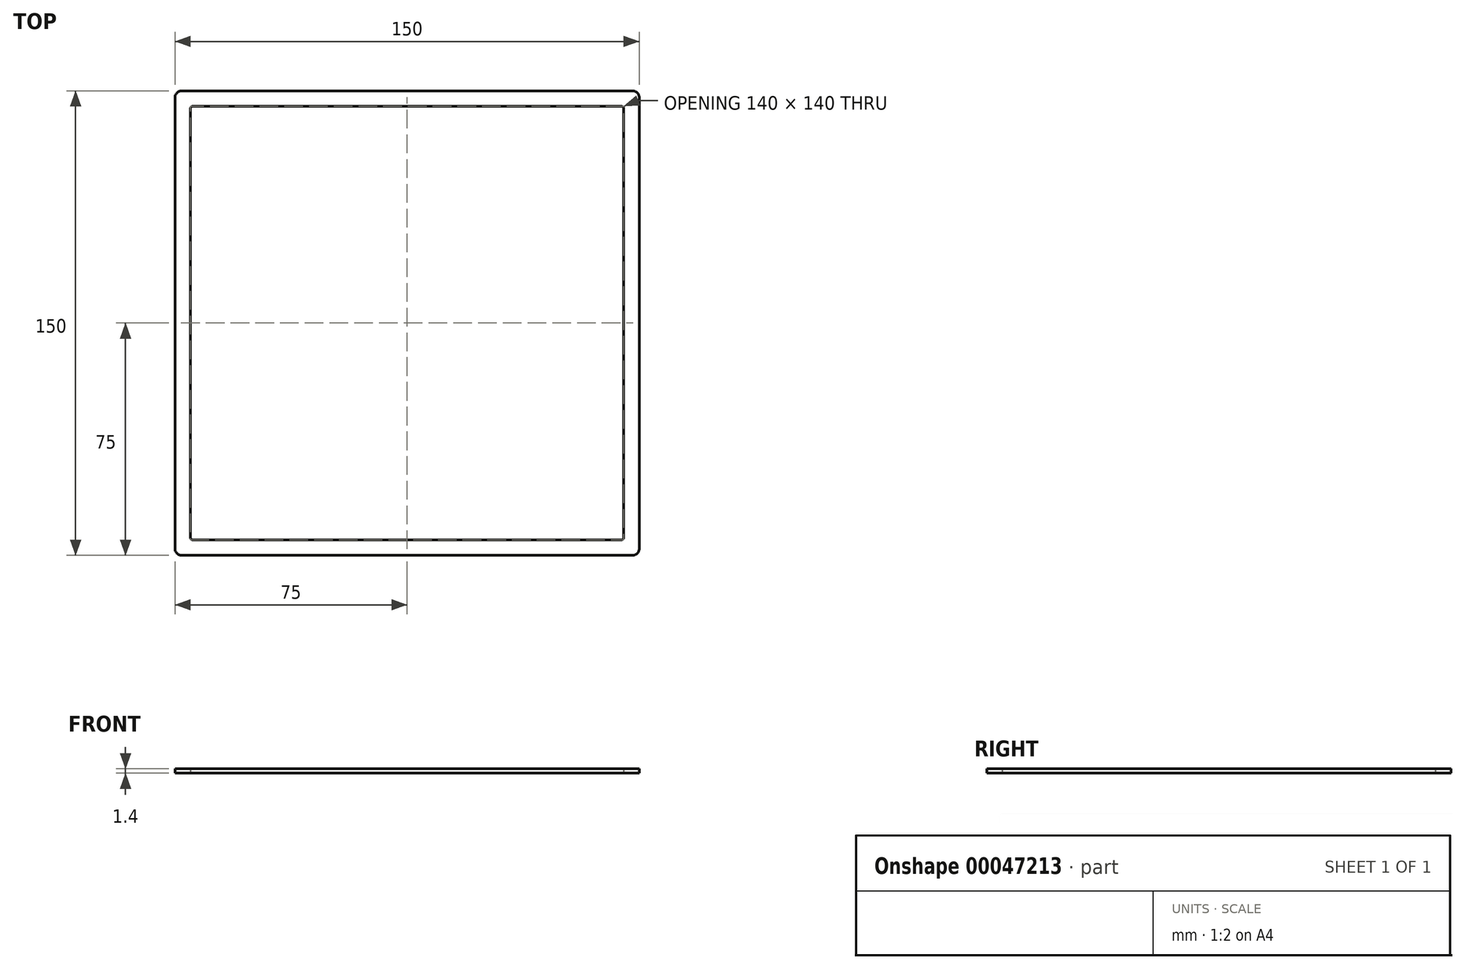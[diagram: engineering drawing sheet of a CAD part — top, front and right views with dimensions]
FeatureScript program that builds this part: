
annotation { "Feature Type Name" : "Feature", "Feature Type Description" : "" }
export const myFeature = defineFeature(function(context is Context, id is Id, definition is map)
    precondition{}
    {
        {
            var Q0;
            Q0=qCreatedBy(makeId("Top.planeOp"),FACE);
            var sketch = newSketch(context, id + "F0", { "sketchPlane" : qUnion([Q0])});
            skLineSegment(sketch, "E0.rect.bottom", {"start": v(75, 75) * mm, "end": v(-75, 75) * mm});
            skLineSegment(sketch, "E0.rect.top", {"start": v(75, -75) * mm, "end": v(-75, -75) * mm});
            skLineSegment(sketch, "E0.rect.left", {"start": v(75, 75) * mm, "end": v(75, -75) * mm});
            skLineSegment(sketch, "E0.rect.right", {"start": v(-75, 75) * mm, "end": v(-75, -75) * mm});
            skPoint(sketch, "E0.rect.middle", {"position": v(0, 0) * mm});
            skLineSegment(sketch, "E1.rect.bottom", {"start": v(70, 70) * mm, "end": v(-70, 70) * mm});
            skLineSegment(sketch, "E1.rect.top", {"start": v(70, -70) * mm, "end": v(-70, -70) * mm});
            skLineSegment(sketch, "E1.rect.left", {"start": v(70, 70) * mm, "end": v(70, -70) * mm});
            skLineSegment(sketch, "E1.rect.right", {"start": v(-70, 70) * mm, "end": v(-70, -70) * mm});
            skSolve(sketch);
        }
        {
            var Q0;
            Q0=makeQuery(id+"F0.imprint","IMPRINT",FACE,{"disambiguationData":[TD([[makeQuery(id+"F0.imprint","IMPRINT",EDGE,{"derivedFrom":sQuery(id+"F0.wireOp",EDGE,"E0.rect.bottom")}),1.0]])]});
            extrude(context, id + "F1", {"entities" : qUnion([Q0]), "depth" : 1.4 * mm});
        }
        {
            var Q0;
            Q0=makeQuery(id+"F1.opExtrude","SWEPT_EDGE",EDGE,{"disambiguationData":[OSD([sQuery(id+"F0.wireOp",EDGE,"E0.rect.bottom"),sQuery(id+"F0.wireOp",EDGE,"E0.rect.left")])]});
            fillet(context, id + "F2", {"entities" : qUnion([Q0]), "radius" : 2.1 * mm, "tangentPropagation" : true, "allowEdgeOverflow" : false});
        }
        {
            var Q0;
            Q0=makeQuery(id+"F1.opExtrude","SWEPT_EDGE",EDGE,{"disambiguationData":[OSD([sQuery(id+"F0.wireOp",EDGE,"E1.rect.bottom"),sQuery(id+"F0.wireOp",EDGE,"E1.rect.left")])]});
            fillet(context, id + "F3", {"entities" : qUnion([Q0]), "radius" : 0.7 * mm, "tangentPropagation" : true, "allowEdgeOverflow" : false});
        }
        {
            var Q0;
            Q0=makeQuery(id+"F1.opExtrude","SWEPT_EDGE",EDGE,{"disambiguationData":[OSD([sQuery(id+"F0.wireOp",EDGE,"E0.rect.bottom"),sQuery(id+"F0.wireOp",EDGE,"E0.rect.right")])]});
            fillet(context, id + "F4", {"entities" : qUnion([Q0]), "radius" : 2.1 * mm, "tangentPropagation" : true, "allowEdgeOverflow" : false});
        }
        {
            var Q0;
            Q0=makeQuery(id+"F1.opExtrude","SWEPT_EDGE",EDGE,{"disambiguationData":[OSD([sQuery(id+"F0.wireOp",EDGE,"E0.rect.top"),sQuery(id+"F0.wireOp",EDGE,"E0.rect.right")])]});
            fillet(context, id + "F5", {"entities" : qUnion([Q0]), "radius" : 2.1 * mm, "tangentPropagation" : true, "allowEdgeOverflow" : false});
        }
        {
            var Q0;
            Q0=makeQuery(id+"F1.opExtrude","SWEPT_EDGE",EDGE,{"disambiguationData":[OSD([sQuery(id+"F0.wireOp",EDGE,"E1.rect.top"),sQuery(id+"F0.wireOp",EDGE,"E1.rect.right")])]});
            fillet(context, id + "F6", {"entities" : qUnion([Q0]), "radius" : 0.7 * mm, "tangentPropagation" : true, "allowEdgeOverflow" : false});
        }
        {
            var Q0;
            Q0=makeQuery(id+"F1.opExtrude","SWEPT_EDGE",EDGE,{"disambiguationData":[OSD([sQuery(id+"F0.wireOp",EDGE,"E0.rect.top"),sQuery(id+"F0.wireOp",EDGE,"E0.rect.left")])]});
            fillet(context, id + "F7", {"entities" : qUnion([Q0]), "radius" : 2.1 * mm, "tangentPropagation" : true, "allowEdgeOverflow" : false});
        }
        {
            var Q0;
            Q0=makeQuery(id+"F1.opExtrude","SWEPT_EDGE",EDGE,{"disambiguationData":[OSD([sQuery(id+"F0.wireOp",EDGE,"E1.rect.top"),sQuery(id+"F0.wireOp",EDGE,"E1.rect.left")])]});
            fillet(context, id + "F8", {"entities" : qUnion([Q0]), "radius" : 0.7 * mm, "tangentPropagation" : true, "allowEdgeOverflow" : false});
        }
        {
            var Q0;
            Q0=makeQuery(id+"F1.opExtrude","SWEPT_EDGE",EDGE,{"disambiguationData":[OSD([sQuery(id+"F0.wireOp",EDGE,"E1.rect.bottom"),sQuery(id+"F0.wireOp",EDGE,"E1.rect.right")])]});
            fillet(context, id + "F9", {"entities" : qUnion([Q0]), "radius" : 0.7 * mm, "tangentPropagation" : true, "allowEdgeOverflow" : false});
        }
    });
